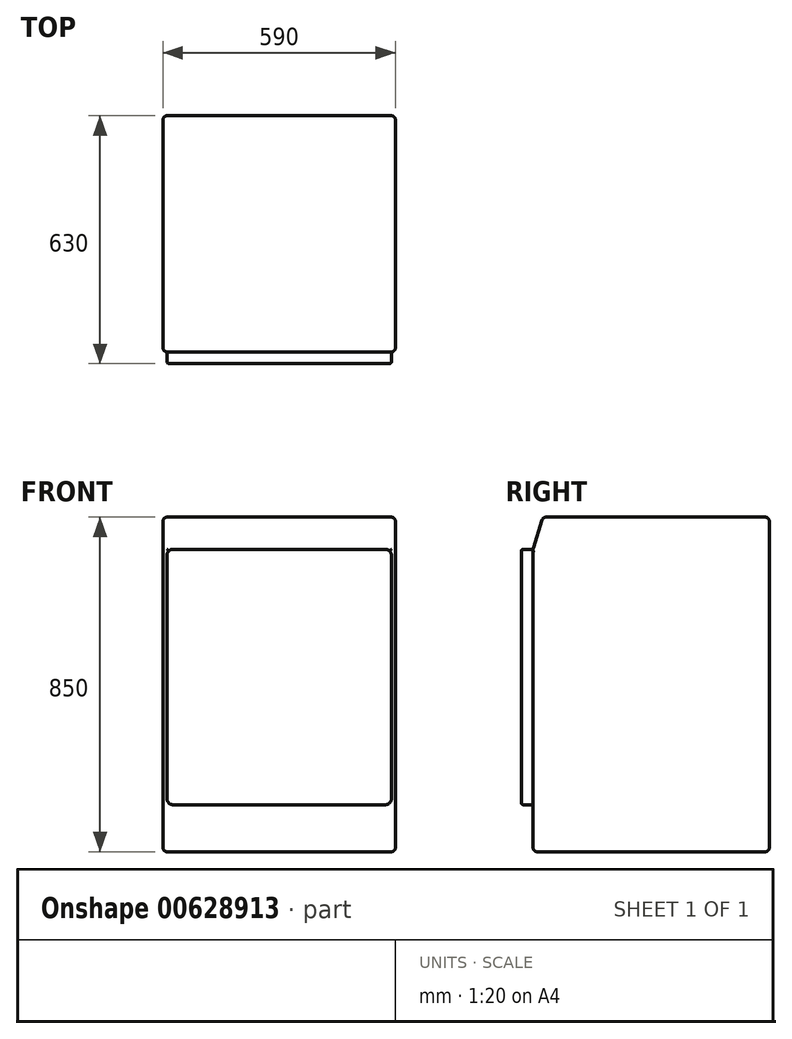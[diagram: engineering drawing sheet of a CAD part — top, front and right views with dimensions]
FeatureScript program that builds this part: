
annotation { "Feature Type Name" : "Feature", "Feature Type Description" : "" }
export const myFeature = defineFeature(function(context is Context, id is Id, definition is map)
    precondition{}
    {
        {
            var Q0;
            Q0=qCreatedBy(makeId("Front.planeOp"),FACE);
            var sketch = newSketch(context, id + "F0", { "sketchPlane" : qUnion([Q0])});
            skLineSegment(sketch, "E0.bottom", {"start": v(0, 0) * mm, "end": v(590, 0) * mm});
            skLineSegment(sketch, "E0.top", {"start": v(0, 850) * mm, "end": v(590, 850) * mm});
            skLineSegment(sketch, "E0.left", {"start": v(0, 0) * mm, "end": v(0, 850) * mm});
            skLineSegment(sketch, "E0.right", {"start": v(590, 0) * mm, "end": v(590, 850) * mm});
            skSolve(sketch);
        }
        {
            var Q0;
            Q0=makeQuery(id+"F0.imprint","IMPRINT",FACE,{"disambiguationData":[TD([[makeQuery(id+"F0.imprint","IMPRINT",EDGE,{"derivedFrom":sQuery(id+"F0.wireOp",EDGE,"E0.bottom")}),1.0]])]});
            extrude(context, id + "F1", {"entities" : qUnion([Q0]), "depth" : 600 * mm, "offsetDistance" : 25 * mm});
        }
        {
            var Q0;
            Q0=makeQuery(id+"F1.opExtrude","CAP_EDGE",EDGE,{"disambiguationData":[OSD([sQuery(id+"F0.wireOp",EDGE,"E0.top")])],"isStart":false});
            chamfer(context, id + "F2", {"entities" : qUnion([Q0]), "chamferType" : ChamferType.TWO_OFFSETS, "width1" : 25 * mm, "oppositeDirection" : false, "width2" : 80 * mm, "tangentPropagation" : true});
        }
        {
            var Q0;
            Q0=makeQuery(id+"F1.opExtrude","CAP_EDGE",EDGE,{"disambiguationData":[OSD([sQuery(id+"F0.wireOp",EDGE,"E0.right")])],"isStart":false});
            var Q1;
            Q1=makeQuery(id+"F1.opExtrude","CAP_EDGE",EDGE,{"disambiguationData":[OSD([sQuery(id+"F0.wireOp",EDGE,"E0.right")])],"isStart":true});
            var Q2;
            Q2=makeQuery(id+"F1.opExtrude","CAP_EDGE",EDGE,{"disambiguationData":[OSD([sQuery(id+"F0.wireOp",EDGE,"E0.left")])],"isStart":false});
            var Q3;
            Q3=makeQuery(id+"F1.opExtrude","CAP_EDGE",EDGE,{"disambiguationData":[OSD([sQuery(id+"F0.wireOp",EDGE,"E0.left")])],"isStart":true});
            var Q4;
            Q4=makeQuery(id+"F1.opExtrude","SWEPT_EDGE",EDGE,{"disambiguationData":[OSD([sQuery(id+"F0.wireOp",EDGE,"E0.bottom"),sQuery(id+"F0.wireOp",EDGE,"E0.left")])]});
            var Q5;
            Q5=makeQuery(id+"F1.opExtrude","CAP_EDGE",EDGE,{"disambiguationData":[OSD([sQuery(id+"F0.wireOp",EDGE,"E0.top")])],"isStart":true});
            var Q6;
            Q6=makeQuery(id+"F1.opExtrude","SWEPT_EDGE",EDGE,{"disambiguationData":[OSD([sQuery(id+"F0.wireOp",EDGE,"E0.top"),sQuery(id+"F0.wireOp",EDGE,"E0.left")])]});
            var Q7;
            Q7=makeQuery(id+"F1.opExtrude","SWEPT_EDGE",EDGE,{"disambiguationData":[OSD([sQuery(id+"F0.wireOp",EDGE,"E0.top"),sQuery(id+"F0.wireOp",EDGE,"E0.right")])]});
            var Q8;
            {var subQ0=sQuery(id+"F0.wireOp",EDGE,"E0.top");Q8=makeQuery(id+"F2.opChamfer","BLEND_EDGE",EDGE,{"blendedFrom":[makeQuery(id+"F1.opExtrude","CAP_EDGE",EDGE,{"disambiguationData":[OSD([subQ0])],"isStart":false}),makeQuery(id+"F1.opExtrude","CAP_FACE",FACE,{"disambiguationData":[OSD([sQuery(id+"F0.wireOp",EDGE,"E0.bottom"),subQ0,sQuery(id+"F0.wireOp",EDGE,"E0.left"),sQuery(id+"F0.wireOp",EDGE,"E0.right")])],"isStart":false})],"blendedInto":[makeQuery(id+"F1.opExtrude","CAP_FACE",FACE,{"disambiguationData":[OSD([sQuery(id+"F0.wireOp",EDGE,"E0.bottom"),subQ0,sQuery(id+"F0.wireOp",EDGE,"E0.left"),sQuery(id+"F0.wireOp",EDGE,"E0.right")])],"isStart":false})]});}
            var Q9;
            {var subQ0=sQuery(id+"F0.wireOp",EDGE,"E0.top");Q9=makeQuery(id+"F2.opChamfer","BLEND_EDGE",EDGE,{"blendedFrom":[makeQuery(id+"F1.opExtrude","CAP_EDGE",EDGE,{"disambiguationData":[OSD([subQ0])],"isStart":false}),makeQuery(id+"F1.opExtrude","SWEPT_FACE",FACE,{"disambiguationData":[OSD([subQ0])]})],"blendedInto":[makeQuery(id+"F1.opExtrude","SWEPT_FACE",FACE,{"disambiguationData":[OSD([subQ0])]})]});}
            var Q10;
            Q10=makeQuery(id+"F1.opExtrude","SWEPT_EDGE",EDGE,{"disambiguationData":[OSD([sQuery(id+"F0.wireOp",EDGE,"E0.bottom"),sQuery(id+"F0.wireOp",EDGE,"E0.right")])]});
            var Q11;
            Q11=makeQuery(id+"F1.opExtrude","CAP_EDGE",EDGE,{"disambiguationData":[OSD([sQuery(id+"F0.wireOp",EDGE,"E0.bottom")])],"isStart":true});
            var Q12;
            Q12=makeQuery(id+"F1.opExtrude","CAP_EDGE",EDGE,{"disambiguationData":[OSD([sQuery(id+"F0.wireOp",EDGE,"E0.bottom")])],"isStart":false});
            var Q13;
            Q13=makeQuery(id+"F2.opChamfer","BLEND_EDGE",EDGE,{"blendedFrom":[makeQuery(id+"F1.opExtrude","CAP_EDGE",EDGE,{"disambiguationData":[OSD([sQuery(id+"F0.wireOp",EDGE,"E0.top")])],"isStart":false}),makeQuery(id+"F1.opExtrude","SWEPT_FACE",FACE,{"disambiguationData":[OSD([sQuery(id+"F0.wireOp",EDGE,"E0.left")])]})],"blendedInto":[makeQuery(id+"F1.opExtrude","SWEPT_FACE",FACE,{"disambiguationData":[OSD([sQuery(id+"F0.wireOp",EDGE,"E0.left")])]})]});
            var Q14;
            Q14=makeQuery(id+"F2.opChamfer","BLEND_EDGE",EDGE,{"blendedFrom":[makeQuery(id+"F1.opExtrude","CAP_EDGE",EDGE,{"disambiguationData":[OSD([sQuery(id+"F0.wireOp",EDGE,"E0.top")])],"isStart":false}),makeQuery(id+"F1.opExtrude","SWEPT_FACE",FACE,{"disambiguationData":[OSD([sQuery(id+"F0.wireOp",EDGE,"E0.right")])]})],"blendedInto":[makeQuery(id+"F1.opExtrude","SWEPT_FACE",FACE,{"disambiguationData":[OSD([sQuery(id+"F0.wireOp",EDGE,"E0.right")])]})]});
            fillet(context, id + "F3", {"entities" : qUnion([Q0, Q1, Q2, Q3, Q4, Q5, Q6, Q7, Q8, Q9, Q10, Q11, Q12, Q13, Q14]), "radius" : 10 * mm, "tangentPropagation" : true, "allowEdgeOverflow" : false});
        }
        {
            var Q0;
            Q0=makeQuery(id+"F1.opExtrude","CAP_FACE",FACE,{"disambiguationData":[OSD([sQuery(id+"F0.wireOp",EDGE,"E0.bottom"),sQuery(id+"F0.wireOp",EDGE,"E0.top"),sQuery(id+"F0.wireOp",EDGE,"E0.left"),sQuery(id+"F0.wireOp",EDGE,"E0.right")])],"isStart":false});
            var sketch = newSketch(context, id + "F4", { "sketchPlane" : qUnion([Q0])});
            skLineSegment(sketch, "E1.bottom", {"start": v(10, 768.47) * mm, "end": v(580, 768.47) * mm});
            skLineSegment(sketch, "E1.top", {"start": v(10, 119.45) * mm, "end": v(580, 119.45) * mm});
            skLineSegment(sketch, "E1.left", {"start": v(10, 768.47) * mm, "end": v(10, 119.45) * mm});
            skLineSegment(sketch, "E1.right", {"start": v(580, 768.47) * mm, "end": v(580, 119.45) * mm});
            skSolve(sketch);
        }
        {
            var Q0;
            Q0=makeQuery(id+"F4.imprint","IMPRINT",FACE,{"disambiguationData":[TD([[makeQuery(id+"F4.imprint","IMPRINT",EDGE,{"derivedFrom":sQuery(id+"F4.wireOp",EDGE,"bNy0Xsj0-mKGA-CEyR-SAA6-0HoSkgoekG0O")}),1.0]])]});
            var Q1;
            Q1=makeQuery(id+"F4.imprint","IMPRINT",FACE,{"disambiguationData":[TD([[makeQuery(id+"F4.imprint","IMPRINT",EDGE,{"derivedFrom":sQuery(id+"F4.wireOp",EDGE,"E1.bottom")}),1.0]])]});
            extrude(context, id + "F5", {"entities" : qUnion([Q0, Q1]), "operationType" : NewBodyOperationType.ADD, "depth" : 30 * mm, "offsetDistance" : 25 * mm});
        }
        {
            var Q0;
            Q0=makeQuery(id+"F5.opExtrude","SWEPT_EDGE",EDGE,{"disambiguationData":[OSD([sQuery(id+"F4.wireOp",EDGE,"E1.bottom"),sQuery(id+"F4.wireOp",EDGE,"E1.left")])]});
            var Q1;
            Q1=makeQuery(id+"F5.opExtrude","SWEPT_EDGE",EDGE,{"disambiguationData":[OSD([sQuery(id+"F0.wireOp",EDGE,"E0.bottom"),sQuery(id+"F0.wireOp",EDGE,"E0.top"),sQuery(id+"F0.wireOp",EDGE,"E0.left"),sQuery(id+"F0.wireOp",EDGE,"E0.right"),sQuery(id+"F4.wireOp",EDGE,"E1.top"),sQuery(id+"F4.wireOp",EDGE,"E1.left")])]});
            var Q2;
            Q2=makeQuery(id+"F5.opExtrude","SWEPT_EDGE",EDGE,{"disambiguationData":[OSD([sQuery(id+"F0.wireOp",EDGE,"E0.bottom"),sQuery(id+"F0.wireOp",EDGE,"E0.top"),sQuery(id+"F0.wireOp",EDGE,"E0.left"),sQuery(id+"F0.wireOp",EDGE,"E0.right"),sQuery(id+"F4.wireOp",EDGE,"E1.top"),sQuery(id+"F4.wireOp",EDGE,"E1.right")])]});
            var Q3;
            Q3=makeQuery(id+"F5.opExtrude","SWEPT_EDGE",EDGE,{"disambiguationData":[OSD([sQuery(id+"F4.wireOp",EDGE,"E1.bottom"),sQuery(id+"F4.wireOp",EDGE,"E1.right")])]});
            fillet(context, id + "F6", {"entities" : qUnion([Q0, Q1, Q2, Q3]), "radius" : 15 * mm, "tangentPropagation" : true, "allowEdgeOverflow" : false});
        }
        {
            var Q0;
            Q0=makeQuery(id+"F5.opExtrude","CAP_FACE",FACE,{"disambiguationData":[OSD([sQuery(id+"F4.wireOp",EDGE,"E1.bottom"),sQuery(id+"F4.wireOp",EDGE,"E1.top"),sQuery(id+"F4.wireOp",EDGE,"E1.left"),sQuery(id+"F4.wireOp",EDGE,"E1.right")])],"isStart":false});
            fillet(context, id + "F7", {"entities" : qUnion([Q0]), "radius" : 5 * mm, "tangentPropagation" : true, "allowEdgeOverflow" : false});
        }
    });
